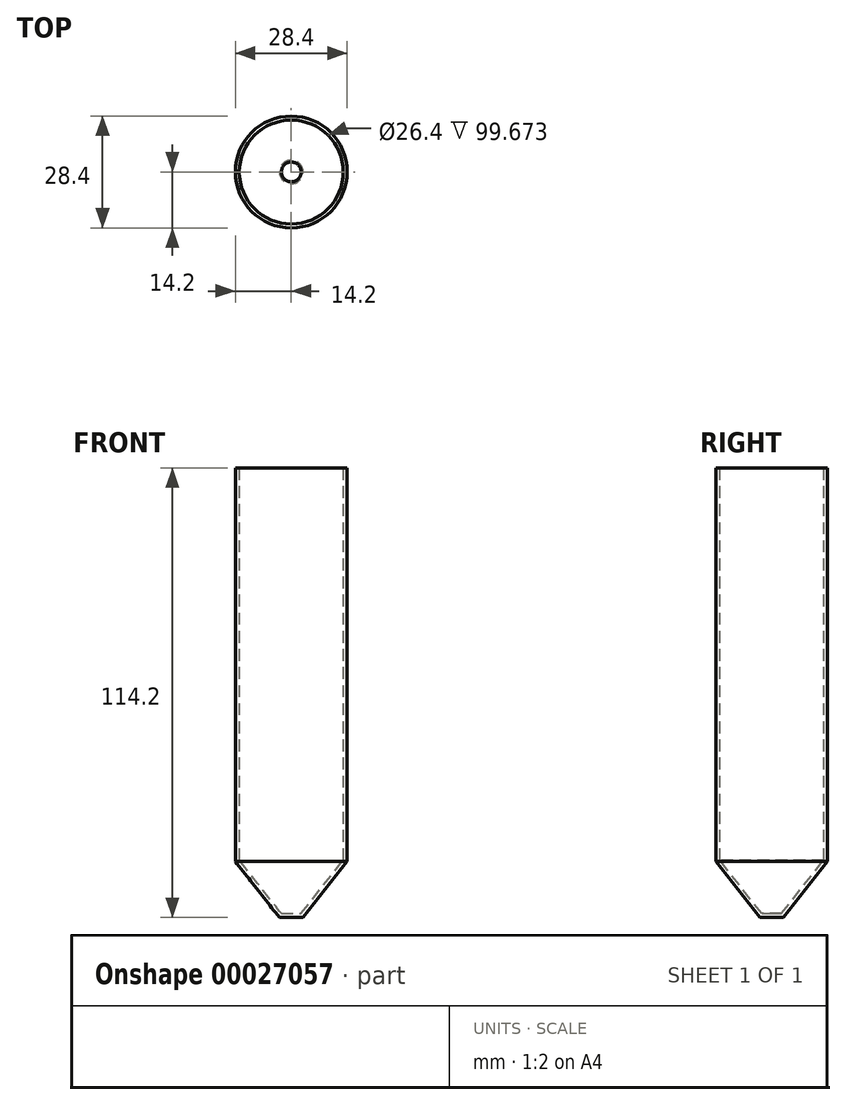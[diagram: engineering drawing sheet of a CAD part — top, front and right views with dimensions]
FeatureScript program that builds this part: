
annotation { "Feature Type Name" : "Feature", "Feature Type Description" : "" }
export const myFeature = defineFeature(function(context is Context, id is Id, definition is map)
    precondition{}
    {
        {
            var Q0;
            Q0=qCreatedBy(makeId("Right.planeOp"),FACE);
            var sketch = newSketch(context, id + "F0", { "sketchPlane" : qUnion([Q0])});
            skLineSegment(sketch, "E0", {"start": v(14.2, 97.59) * mm, "end": v(14.2, -2.43) * mm});
            skLineSegment(sketch, "E1", {"start": v(14.2, -2.43) * mm, "end": v(3, -16.61) * mm});
            skLineSegment(sketch, "E2", {"start": v(3, -16.61) * mm, "end": v(0, -16.61) * mm});
            skLineSegment(sketch, "E3", {"start": v(0, -16.61) * mm, "end": v(0, 97.59) * mm, "construction": true});
            skLineSegment(sketch, "E4", {"start": v(0, 97.59) * mm, "end": v(14.2, 97.59) * mm, "construction": true});
            skLineSegment(sketch, "E5.0", {"start": v(2.52, -15.61) * mm, "end": v(0, -15.61) * mm});
            skLineSegment(sketch, "E5.1", {"start": v(13.2, -2.09) * mm, "end": v(2.52, -15.61) * mm});
            skLineSegment(sketch, "E5.2", {"start": v(13.2, 97.59) * mm, "end": v(13.2, -2.09) * mm});
            skLineSegment(sketch, "E6", {"start": v(0, -16.61) * mm, "end": v(0, -15.61) * mm});
            skLineSegment(sketch, "E7", {"start": v(13.2, 97.59) * mm, "end": v(14.2, 97.59) * mm});
            skSolve(sketch);
        }
        {
            var Q0;
            Q0=makeQuery(id+"F0.imprint","IMPRINT",FACE,{"disambiguationData":[TD([[makeQuery(id+"F0.imprint","IMPRINT",EDGE,{"derivedFrom":sQuery(id+"F0.wireOp",EDGE,"E0")}),-1.0]])]});
            var Q1;
            Q1=sQuery(id+"F0.wireOp",EDGE,"E3");
            revolve(context, id + "F1", {"entities" : qUnion([Q0]), "axis" : qUnion([Q1]), "revolveType" : RevolveType.FULL});
        }
    });
